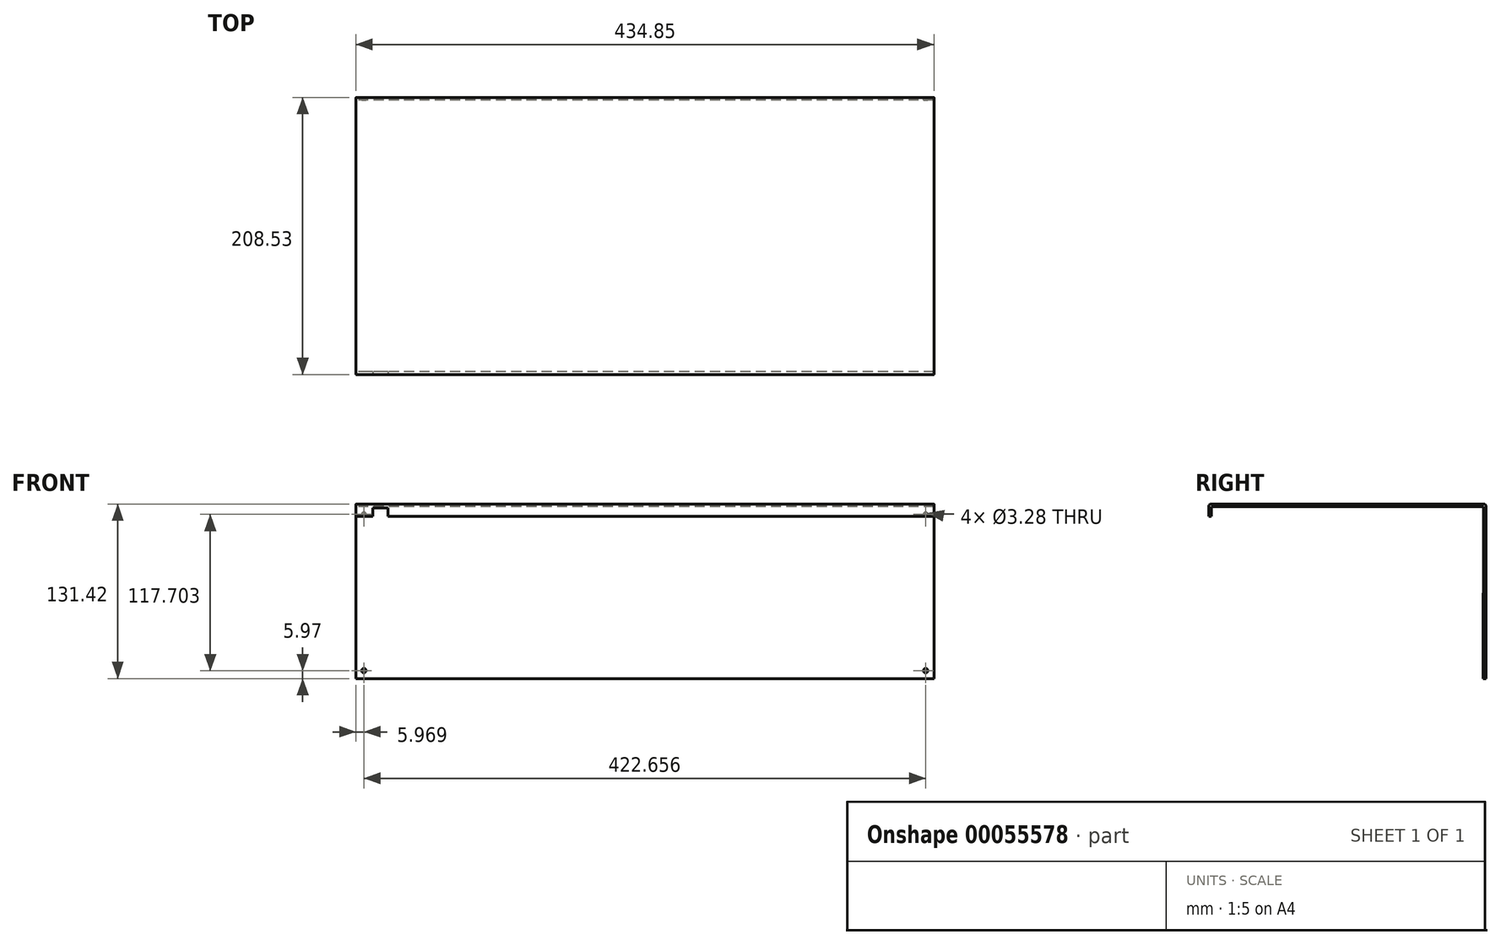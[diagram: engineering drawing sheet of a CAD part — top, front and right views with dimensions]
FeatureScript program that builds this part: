
annotation { "Feature Type Name" : "Feature", "Feature Type Description" : "" }
export const myFeature = defineFeature(function(context is Context, id is Id, definition is map)
    precondition{}
    {
        {
            var Q0;
            Q0=qCreatedBy(makeId("Right.planeOp"),FACE);
            var sketch = newSketch(context, id + "F0", { "sketchPlane" : qUnion([Q0])});
            skLineSegment(sketch, "E0", {"start": v(-1.78, 0) * mm, "end": v(-206.76, 0) * mm});
            skLineSegment(sketch, "E1", {"start": v(-208.53, -1.78) * mm, "end": v(-208.53, -9.14) * mm});
            skLineSegment(sketch, "E2", {"start": v(-2.03, -131.42) * mm, "end": v(0, -131.42) * mm});
            skLineSegment(sketch, "E3", {"start": v(0, -131.42) * mm, "end": v(0, -1.78) * mm});
            skLineSegment(sketch, "E4", {"start": v(-2.03, -131.42) * mm, "end": v(-1.96, -2.03) * mm});
            skLineSegment(sketch, "E5", {"start": v(-208.53, -9.14) * mm, "end": v(-206.5, -9.14) * mm});
            skLineSegment(sketch, "E6", {"start": v(-1.96, -2.03) * mm, "end": v(-206.5, -2.03) * mm});
            skLineSegment(sketch, "E7", {"start": v(-206.5, -2.03) * mm, "end": v(-206.5, -9.14) * mm});
            skPoint(sketch, "E8.visualSharp", {"position": v(-208.53, 0) * mm});
            skArc(sketch, "E8.filletArc", {"start": v(-206.76, 0) * mm, "mid": v(-208.01, -0.52) * mm, "end": v(-208.53, -1.78) * mm});
            skPoint(sketch, "E9.visualSharp", {"position": v(0, 0) * mm});
            skArc(sketch, "E9.filletArc", {"start": v(0, -1.78) * mm, "mid": v(-0.52, -0.52) * mm, "end": v(-1.78, 0) * mm});
            skSolve(sketch);
        }
        {
            var Q0;
            Q0 = qSketchRegion(id + "F0", true);
            extrude(context, id + "F1", {"entities" : qUnion([Q0]), "depth" : 434.85 * mm});
        }
        {
            var Q0;
            Q0=makeQuery(id+"F1.opExtrude","SWEPT_FACE",FACE,{"disambiguationData":[OSD([sQuery(id+"F0.wireOp",EDGE,"E1")])]});
            var sketch = newSketch(context, id + "F2", { "sketchPlane" : qUnion([Q0])});
            skLineSegment(sketch, "E10", {"start": v(12.57, -2.8) * mm, "end": v(12.57, -9.14) * mm});
            skLineSegment(sketch, "E11", {"start": v(12.57, -2.8) * mm, "end": v(23.97, -2.8) * mm});
            skLineSegment(sketch, "E12", {"start": v(23.97, -2.8) * mm, "end": v(23.97, -9.14) * mm});
            skLineSegment(sketch, "E13", {"start": v(23.97, -9.14) * mm, "end": v(12.57, -9.14) * mm});
            skSolve(sketch);
        }
        {
            var Q0;
            Q0=makeQuery(id+"F2.imprint","IMPRINT",FACE,{"disambiguationData":[TD([[makeQuery(id+"F2.imprint","IMPRINT",EDGE,{"derivedFrom":sQuery(id+"F2.wireOp",EDGE,"E10")}),1.0]])]});
            extrude(context, id + "F3", {"entities" : qUnion([Q0]), "operationType" : NewBodyOperationType.REMOVE, "oppositeDirection" : true, "depth" : 25.4 * mm});
        }
        {
            var Q0;
            Q0=makeQuery(id+"F1.opExtrude","SWEPT_FACE",FACE,{"disambiguationData":[OSD([sQuery(id+"F0.wireOp",EDGE,"E4")])]});
            var sketch = newSketch(context, id + "F4", { "sketchPlane" : qUnion([Q0])});
            skCircle(sketch, "E14", {"center": v(5.97, -125.45) * mm, "radius": 1.64 * mm});
            skCircle(sketch, "E15", {"center": v(428.63, -125.45) * mm, "radius": 1.64 * mm});
            skSolve(sketch);
        }
        {
            var Q0;
            Q0=makeQuery(id+"F4.imprint","IMPRINT",FACE,{"disambiguationData":[TD([[makeQuery(id+"F4.imprint","IMPRINT",EDGE,{"derivedFrom":sQuery(id+"F4.wireOp",EDGE,"E14")}),1.0]])]});
            var Q1;
            Q1=makeQuery(id+"F4.imprint","IMPRINT",FACE,{"disambiguationData":[TD([[makeQuery(id+"F4.imprint","IMPRINT",EDGE,{"derivedFrom":sQuery(id+"F4.wireOp",EDGE,"E15")}),1.0]])]});
            extrude(context, id + "F5", {"entities" : qUnion([Q0, Q1]), "operationType" : NewBodyOperationType.REMOVE, "oppositeDirection" : true, "depth" : 25.4 * mm});
        }
        {
            var Q0;
            Q0=makeQuery(id+"F1.opExtrude","SWEPT_FACE",FACE,{"disambiguationData":[OSD([sQuery(id+"F0.wireOp",EDGE,"E3")])]});
            var sketch = newSketch(context, id + "F6", { "sketchPlane" : qUnion([Q0])});
            skCircle(sketch, "E16", {"center": v(-428.63, -7.75) * mm, "radius": 1.64 * mm});
            skCircle(sketch, "E17", {"center": v(-5.97, -7.75) * mm, "radius": 1.64 * mm});
            skSolve(sketch);
        }
        {
            var Q0;
            Q0 = qSketchRegion(id + "F6", true);
            extrude(context, id + "F7", {"entities" : qUnion([Q0]), "operationType" : NewBodyOperationType.REMOVE, "oppositeDirection" : true, "depth" : 25.4 * mm});
        }
    });
